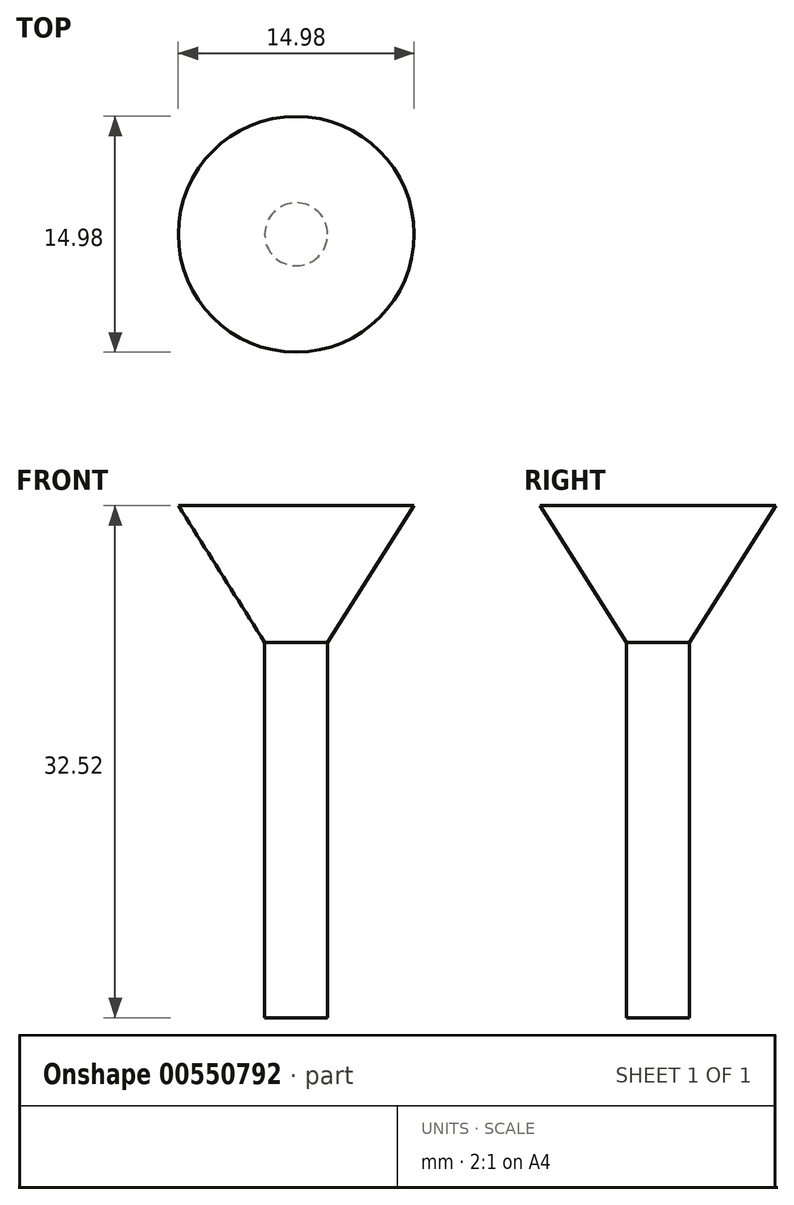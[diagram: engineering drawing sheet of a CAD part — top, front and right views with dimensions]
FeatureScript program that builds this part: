
annotation { "Feature Type Name" : "Feature", "Feature Type Description" : "" }
export const myFeature = defineFeature(function(context is Context, id is Id, definition is map)
    precondition{}
    {
        {
            var Q0;
            Q0=qCreatedBy(makeId("Right.planeOp"),FACE);
            var sketch = newSketch(context, id + "F0", { "sketchPlane" : qUnion([Q0])});
            skLineSegment(sketch, "E0", {"start": v(0, 0) * mm, "end": v(2, 0) * mm});
            skLineSegment(sketch, "E1", {"start": v(2, 0) * mm, "end": v(2, 23.85) * mm});
            skLineSegment(sketch, "E2", {"start": v(2, 23.85) * mm, "end": v(7.49, 32.52) * mm});
            skLineSegment(sketch, "E3", {"start": v(7.49, 32.52) * mm, "end": v(0, 32.52) * mm});
            skLineSegment(sketch, "E4", {"start": v(0, 32.52) * mm, "end": v(0, 0) * mm});
            skSolve(sketch);
        }
        {
            var Q0;
            Q0=sQuery(id+"F0.wireOp",EDGE,"E3");
            var Q1;
            Q1=sQuery(id+"F0.wireOp",EDGE,"E2");
            var Q2;
            Q2=sQuery(id+"F0.wireOp",EDGE,"E1");
            var Q3;
            Q3=sQuery(id+"F0.wireOp",EDGE,"E0");
            var Q4;
            Q4=sQuery(id+"F0.wireOp",EDGE,"E4");
            revolve(context, id + "F1", {"bodyType" : ToolBodyType.SURFACE, "surfaceEntities" : qUnion([Q0, Q1, Q2, Q3]), "axis" : qUnion([Q4]), "revolveType" : RevolveType.FULL});
        }
    });
